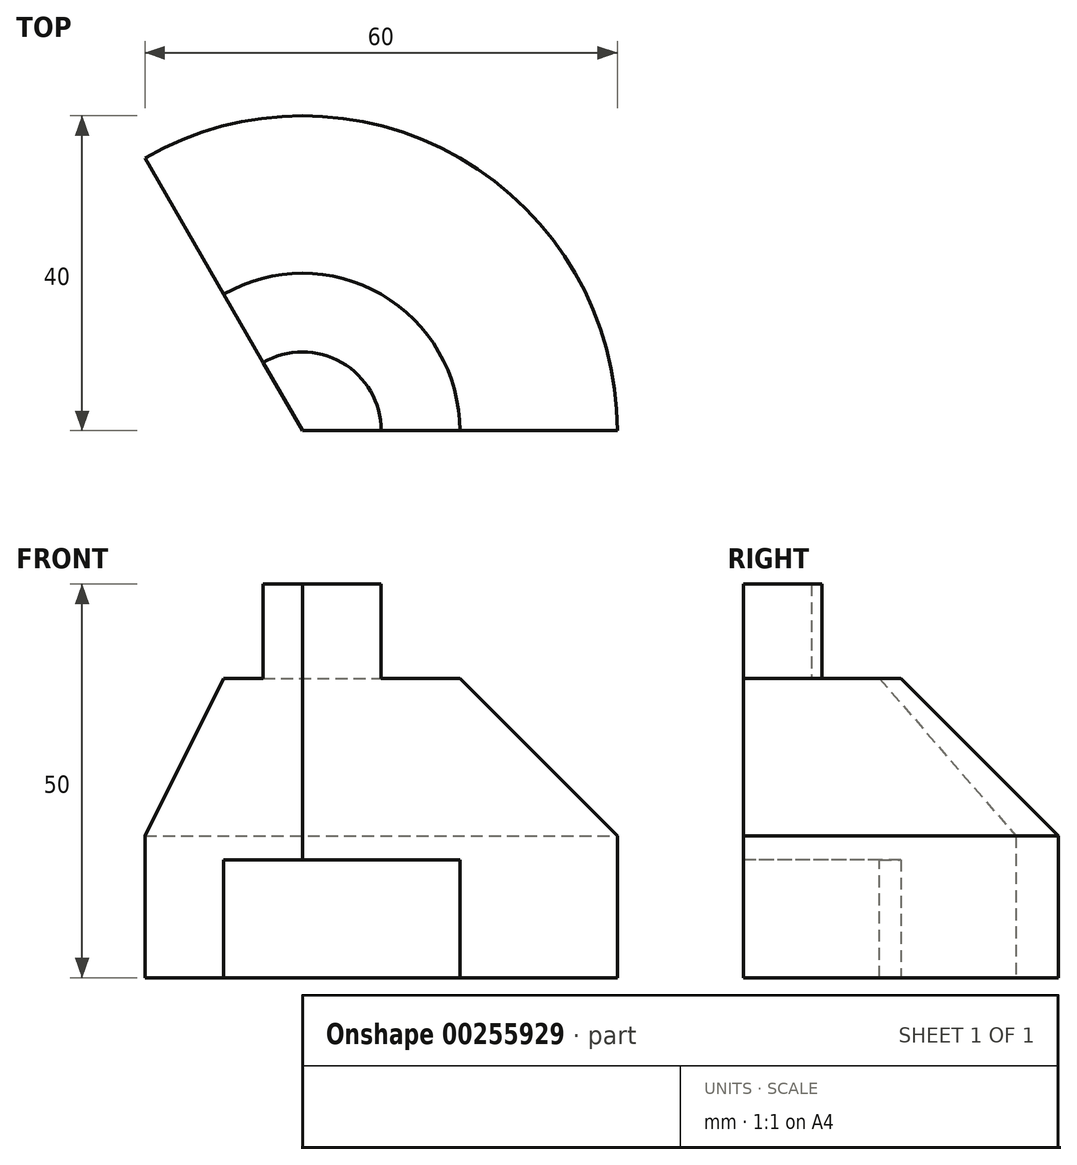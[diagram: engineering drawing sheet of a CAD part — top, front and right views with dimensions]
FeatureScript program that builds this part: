
annotation { "Feature Type Name" : "Feature", "Feature Type Description" : "" }
export const myFeature = defineFeature(function(context is Context, id is Id, definition is map)
    precondition{}
    {
        {
            var Q0;
            Q0=qCreatedBy(makeId("Front.planeOp"),FACE);
            var sketch = newSketch(context, id + "F0", { "sketchPlane" : qUnion([Q0])});
            skLineSegment(sketch, "E0", {"start": v(0, 35) * mm, "end": v(10, 35) * mm});
            skLineSegment(sketch, "E1", {"start": v(10, 35) * mm, "end": v(10, 23) * mm});
            skLineSegment(sketch, "E2", {"start": v(10, 23) * mm, "end": v(20, 23) * mm});
            skLineSegment(sketch, "E3", {"start": v(20, 23) * mm, "end": v(40, 3) * mm});
            skLineSegment(sketch, "E4", {"start": v(40, 3) * mm, "end": v(40, -15) * mm});
            skLineSegment(sketch, "E5", {"start": v(40, -15) * mm, "end": v(20, -15) * mm});
            skLineSegment(sketch, "E6", {"start": v(20, -15) * mm, "end": v(20, 0) * mm});
            skLineSegment(sketch, "E7", {"start": v(20, 0) * mm, "end": v(0, 0) * mm});
            skLineSegment(sketch, "E8", {"start": v(0, 0) * mm, "end": v(0, 35) * mm});
            skSolve(sketch);
        }
        {
            var Q0;
            Q0=makeQuery(id+"F0.imprint","IMPRINT",FACE,{"disambiguationData":[TD([[makeQuery(id+"F0.imprint","IMPRINT",EDGE,{"derivedFrom":sQuery(id+"F0.wireOp",EDGE,"E0")}),-1.0]])]});
            var Q1;
            Q1=sQuery(id+"F0.wireOp",EDGE,"E8");
            revolve(context, id + "F1", {"entities" : qUnion([Q0]), "axis" : qUnion([Q1]), "revolveType" : RevolveType.ONE_DIRECTION, "angle" : 120 * degree});
        }
    });
